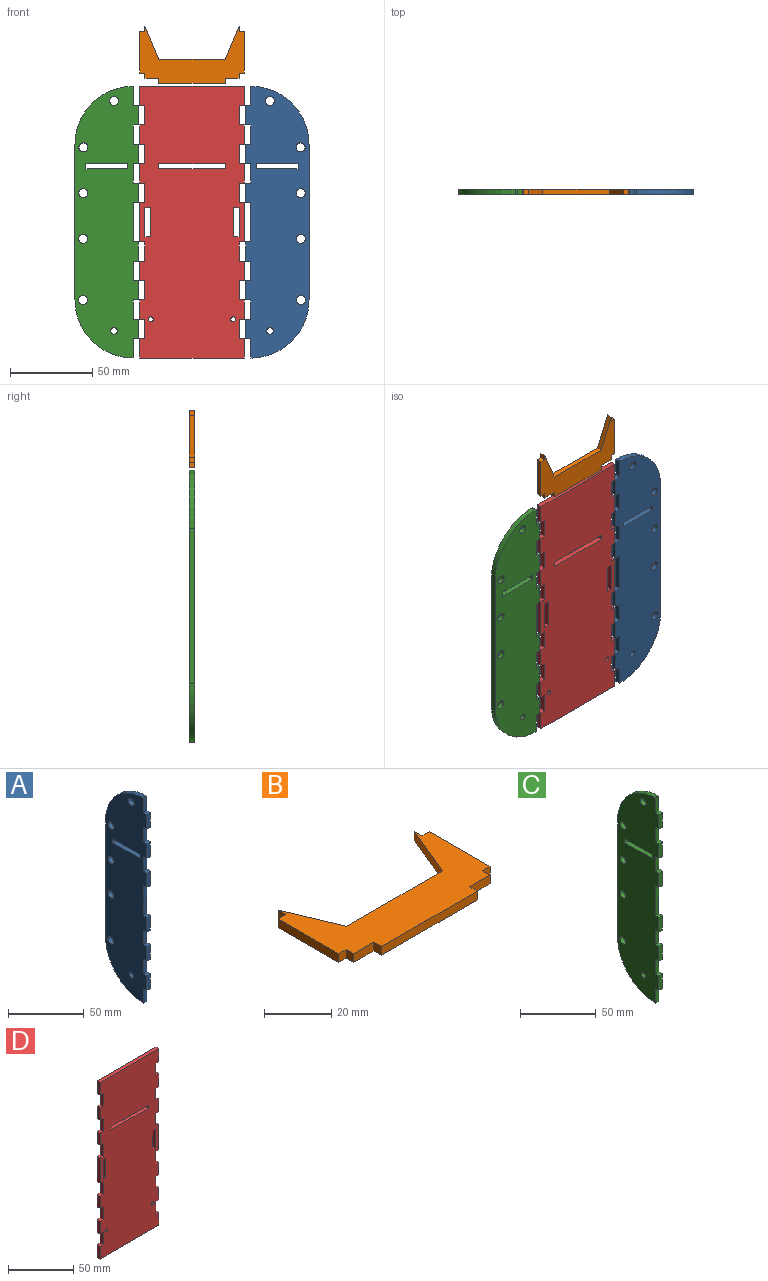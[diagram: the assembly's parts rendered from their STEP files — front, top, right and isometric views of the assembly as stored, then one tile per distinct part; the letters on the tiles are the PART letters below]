
ASSEMBLY  parts=4 mates=5
PART A: 42 faces, bbox 3.2x38.5x165.1 mm
  f0: plane 165.1x38.45mm, normal (1,0,0), area 5303.1mm2, adj f1,f2,f3,f4,f5,f6,f7,f8
  f1: plane 3.18x3.18mm, normal (0,0,1), area 10.1mm2, adj f0,f2,f28,f31
  f2: plane 11.76x3.18mm, normal (0,-1,0), area 37.3mm2, adj f0,f1,f3,f28
  f3: plane 3.18x3.18mm, normal (0,0,-1), area 10.1mm2, adj f0,f2,f4,f28
  f4: plane 11.76x3.18mm, normal (0,-1,0), area 37.3mm2, adj f0,f3,f5,f28
  f5: plane 3.18x3.18mm, normal (0,0,1), area 10.1mm2, adj f0,f4,f6,f28
  f6: plane 11.76x3.18mm, normal (0,-1,0), area 37.3mm2, adj f0,f5,f7,f28
  f7: plane 3.18x3.18mm, normal (0,0,-1), area 10.1mm2, adj f0,f6,f8,f28
  f8: plane 11.76x3.18mm, normal (0,-1,0), area 37.3mm2, adj f0,f7,f9,f28
  f9: plane 3.18x0.97mm, normal (0,0,-1), area 3.1mm2, adj f0,f8,f10,f28
  f10: cylinder r=35.28mm len=35.27mm, axis (-1,0,0), area 172.9mm2, adj f0,f9,f11,f28
  f11: plane 94.57x3.18mm, normal (0,1,0), area 300.3mm2, adj f0,f10,f12,f28
  f12: cylinder r=35.28mm len=35.27mm, axis (-1,0,0), area 172.9mm2, adj f0,f11,f13,f28
  f13: plane 3.18x0.97mm, normal (0,0,1), area 3.1mm2, adj f0,f12,f14,f28
  f14: plane 11.76x3.18mm, normal (0,-1,0), area 37.3mm2, adj f0,f13,f15,f28
  f15: plane 3.18x3.18mm, normal (0,0,1), area 10.1mm2, adj f0,f14,f16,f28
  f16: plane 11.76x3.18mm, normal (0,-1,0), area 37.3mm2, adj f0,f15,f17,f28
  f17: plane 3.18x3.18mm, normal (0,0,-1), area 10.1mm2, adj f0,f16,f18,f28
  f18: plane 11.76x3.18mm, normal (0,-1,0), area 37.3mm2, adj f0,f17,f19,f28
  f19: plane 3.18x3.18mm, normal (0,0,1), area 10.1mm2, adj f0,f18,f20,f28
  f20: plane 11.76x3.18mm, normal (0,-1,0), area 37.3mm2, adj f0,f19,f21,f28
  f21: plane 3.18x3.18mm, normal (0,0,-1), area 10.1mm2, adj f0,f20,f22,f28
  f22: plane 11.76x3.18mm, normal (0,-1,0), area 37.3mm2, adj f0,f21,f23,f28
  f23: plane 3.18x3.18mm, normal (0,0,1), area 10.1mm2, adj f0,f22,f24,f28
  f24: plane 11.76x3.18mm, normal (0,-1,0), area 37.3mm2, adj f0,f23,f25,f28
  f25: plane 3.18x3.18mm, normal (0,0,-1), area 10.1mm2, adj f0,f24,f26,f28
  f26: plane 24.04x3.18mm, normal (0,-1,0), area 76.3mm2, adj f0,f25,f27,f28
  f27: plane 3.18x3.18mm, normal (0,0,1), area 10.1mm2, adj f0,f26,f28,f30
  f28: plane 165.1x38.45mm, normal (-1,0,0), area 5303.1mm2, adj f1,f2,f3,f4,f5,f6,f7,f8
  f29: cylinder r=2.75mm len=5.5mm, axis (-1,0,0), area 54.9mm2, adj f0,f28
  f30: plane 11.76x3.18mm, normal (0,-1,0), area 37.3mm2, adj f0,f27,f28,f32
  f31: plane 11.76x3.18mm, normal (0,-1,0), area 37.3mm2, adj f0,f1,f28,f32
  f32: plane 3.18x3.18mm, normal (0,0,-1), area 10.1mm2, adj f0,f28,f30,f31
  f33: cylinder r=2.75mm len=5.5mm, axis (-1,0,0), area 54.9mm2, adj f0,f28
  f34: cylinder r=2mm len=4mm, axis (-1,0,0), area 39.9mm2, adj f0,f28
  f35: cylinder r=2.75mm len=5.5mm, axis (-1,0,0), area 54.9mm2, adj f0,f28
  f36: cylinder r=2.75mm len=5.5mm, axis (-1,0,0), area 54.9mm2, adj f0,f28
  f37: cylinder r=2.75mm len=5.5mm, axis (-1,0,0), area 54.9mm2, adj f0,f28
  f38: plane 25.4x3.18mm, normal (0,0,1), area 80.6mm2, adj f0,f28,f40,f41
  f39: plane 25.4x3.18mm, normal (0,0,-1), area 80.6mm2, adj f0,f28,f40,f41
  f40: plane 3.18x3.18mm, normal (0,1,0), area 10.1mm2, adj f0,f28,f38,f39
  f41: plane 3.18x3.18mm, normal (0,-1,0), area 10.1mm2, adj f0,f28,f38,f39
PART B: 20 faces, bbox 63.5x34.9x3.2 mm
  f0: plane 63.5x34.93mm, normal (0,0,-1), area 1117.7mm2, adj f2,f3,f4,f5,f6,f7,f8,f9
  f1: plane 63.5x34.93mm, normal (0,0,1), area 1117.7mm2, adj f2,f3,f4,f5,f6,f7,f8,f9
  f2: plane 20.25x8.47mm, normal (0.92,0.39,0), area 69.7mm2, adj f0,f1,f3,f18
  f3: plane 3.18x3.18mm, normal (-1,0,0), area 10.1mm2, adj f0,f1,f2,f4
  f4: plane 3.18x3.18mm, normal (0,1,0), area 10.1mm2, adj f0,f1,f3,f5
  f5: plane 25.4x3.18mm, normal (-1,0,0), area 80.6mm2, adj f0,f1,f4,f6
  f6: plane 3.18x3.18mm, normal (0,-1,0), area 10.1mm2, adj f0,f1,f5,f7
  f7: plane 3.18x3.18mm, normal (-1,0,0), area 10.1mm2, adj f0,f1,f6,f8
  f8: plane 8.47x3.18mm, normal (0,-1,0), area 26.9mm2, adj f0,f1,f7,f9
  f9: plane 3.18x3.18mm, normal (-1,0,0), area 10.1mm2, adj f0,f1,f8,f10
  f10: plane 40.22x3.18mm, normal (0,-1,0), area 127.7mm2, adj f0,f1,f9,f11
  f11: plane 3.18x3.18mm, normal (1,0,0), area 10.1mm2, adj f0,f1,f10,f12
  f12: plane 8.47x3.18mm, normal (0,-1,0), area 26.9mm2, adj f0,f1,f11,f13
  f13: plane 3.18x3.18mm, normal (1,0,0), area 10.1mm2, adj f0,f1,f12,f14
  f14: plane 3.18x3.18mm, normal (0,-1,0), area 10.1mm2, adj f0,f1,f13,f15
  f15: plane 25.4x3.18mm, normal (1,0,0), area 80.6mm2, adj f0,f1,f14,f16
  f16: plane 3.18x3.18mm, normal (0,1,0), area 10.1mm2, adj f0,f1,f15,f17
  f17: plane 3.18x3.18mm, normal (1,0,0), area 10.1mm2, adj f0,f1,f16,f19
  f18: plane 40.22x3.18mm, normal (0,1,0), area 127.7mm2, adj f0,f1,f2,f19
  f19: plane 20.25x8.47mm, normal (-0.92,0.39,0), area 69.7mm2, adj f0,f1,f17,f18
PART C: 42 faces, bbox 3.2x38.5x165.1 mm
  f0: plane 165.1x38.45mm, normal (-1,0,0), area 5303.1mm2, adj f1,f2,f3,f4,f5,f6,f7,f8
  f1: plane 3.18x3.18mm, normal (0,0,1), area 10.1mm2, adj f0,f2,f28,f31
  f2: plane 11.76x3.18mm, normal (0,-1,0), area 37.3mm2, adj f0,f1,f3,f28
  f3: plane 3.18x3.18mm, normal (0,0,-1), area 10.1mm2, adj f0,f2,f4,f28
  f4: plane 11.76x3.18mm, normal (0,-1,0), area 37.3mm2, adj f0,f3,f5,f28
  f5: plane 3.18x3.18mm, normal (0,0,1), area 10.1mm2, adj f0,f4,f6,f28
  f6: plane 11.76x3.18mm, normal (0,-1,0), area 37.3mm2, adj f0,f5,f7,f28
  f7: plane 3.18x3.18mm, normal (0,0,-1), area 10.1mm2, adj f0,f6,f8,f28
  f8: plane 11.76x3.18mm, normal (0,-1,0), area 37.3mm2, adj f0,f7,f9,f28
  f9: plane 3.18x0.97mm, normal (0,0,-1), area 3.1mm2, adj f0,f8,f10,f28
  f10: cylinder r=35.28mm len=35.27mm, axis (1,0,0), area 172.9mm2, adj f0,f9,f11,f28
  f11: plane 94.57x3.18mm, normal (0,1,0), area 300.3mm2, adj f0,f10,f12,f28
  f12: cylinder r=35.28mm len=35.27mm, axis (1,0,0), area 172.9mm2, adj f0,f11,f13,f28
  f13: plane 3.18x0.97mm, normal (0,0,1), area 3.1mm2, adj f0,f12,f14,f28
  f14: plane 11.76x3.18mm, normal (0,-1,0), area 37.3mm2, adj f0,f13,f15,f28
  f15: plane 3.18x3.18mm, normal (0,0,1), area 10.1mm2, adj f0,f14,f16,f28
  f16: plane 11.76x3.18mm, normal (0,-1,0), area 37.3mm2, adj f0,f15,f17,f28
  f17: plane 3.18x3.18mm, normal (0,0,-1), area 10.1mm2, adj f0,f16,f18,f28
  f18: plane 11.76x3.18mm, normal (0,-1,0), area 37.3mm2, adj f0,f17,f19,f28
  f19: plane 3.18x3.18mm, normal (0,0,1), area 10.1mm2, adj f0,f18,f20,f28
  f20: plane 11.76x3.18mm, normal (0,-1,0), area 37.3mm2, adj f0,f19,f21,f28
  f21: plane 3.18x3.18mm, normal (0,0,-1), area 10.1mm2, adj f0,f20,f22,f28
  f22: plane 11.76x3.18mm, normal (0,-1,0), area 37.3mm2, adj f0,f21,f23,f28
  f23: plane 3.18x3.18mm, normal (0,0,1), area 10.1mm2, adj f0,f22,f24,f28
  f24: plane 11.76x3.18mm, normal (0,-1,0), area 37.3mm2, adj f0,f23,f25,f28
  f25: plane 3.18x3.18mm, normal (0,0,-1), area 10.1mm2, adj f0,f24,f26,f28
  f26: plane 24.04x3.18mm, normal (0,-1,0), area 76.3mm2, adj f0,f25,f27,f28
  f27: plane 3.18x3.18mm, normal (0,0,1), area 10.1mm2, adj f0,f26,f28,f30
  f28: plane 165.1x38.45mm, normal (1,0,0), area 5303.1mm2, adj f1,f2,f3,f4,f5,f6,f7,f8
  f29: cylinder r=2.75mm len=5.5mm, axis (1,0,0), area 54.9mm2, adj f0,f28
  f30: plane 11.76x3.18mm, normal (0,-1,0), area 37.3mm2, adj f0,f27,f28,f32
  f31: plane 11.76x3.18mm, normal (0,-1,0), area 37.3mm2, adj f0,f1,f28,f32
  f32: plane 3.18x3.18mm, normal (0,0,-1), area 10.1mm2, adj f0,f28,f30,f31
  f33: cylinder r=2.75mm len=5.5mm, axis (1,0,0), area 54.9mm2, adj f0,f28
  f34: cylinder r=2mm len=4mm, axis (1,0,0), area 39.9mm2, adj f0,f28
  f35: cylinder r=2.75mm len=5.5mm, axis (1,0,0), area 54.9mm2, adj f0,f28
  f36: cylinder r=2.75mm len=5.5mm, axis (1,0,0), area 54.9mm2, adj f0,f28
  f37: cylinder r=2.75mm len=5.5mm, axis (1,0,0), area 54.9mm2, adj f0,f28
  f38: plane 25.4x3.18mm, normal (0,0,1), area 80.6mm2, adj f0,f28,f40,f41
  f39: plane 25.4x3.18mm, normal (0,0,-1), area 80.6mm2, adj f0,f28,f40,f41
  f40: plane 3.18x3.18mm, normal (0,-1,0), area 10.1mm2, adj f0,f28,f38,f39
  f41: plane 3.18x3.18mm, normal (0,1,0), area 10.1mm2, adj f0,f28,f38,f39
PART D: 68 faces, bbox 63.5x3.2x165.1 mm
  f0: plane 11.76x3.18mm, normal (1,0,0), area 37.3mm2, adj f1,f58,f62,f63
  f1: plane 63.5x3.18mm, normal (0,0,1), area 201.6mm2, adj f0,f2,f62,f63
  f2: plane 11.76x3.18mm, normal (-1,0,0), area 37.3mm2, adj f1,f3,f62,f63
  f3: plane 3.18x3.18mm, normal (0,0,-1), area 10.1mm2, adj f2,f4,f62,f63
  f4: plane 11.76x3.18mm, normal (-1,0,0), area 37.3mm2, adj f3,f5,f62,f63
  f5: plane 3.18x3.18mm, normal (0,0,1), area 10.1mm2, adj f4,f6,f62,f63
  f6: plane 11.76x3.18mm, normal (-1,0,0), area 37.3mm2, adj f5,f7,f62,f63
  f7: plane 3.18x3.18mm, normal (0,0,-1), area 10.1mm2, adj f6,f8,f62,f63
  f8: plane 11.76x3.18mm, normal (-1,0,0), area 37.3mm2, adj f7,f9,f62,f63
  f9: plane 3.18x3.18mm, normal (0,0,1), area 10.1mm2, adj f8,f10,f62,f63
  f10: plane 11.76x3.18mm, normal (-1,0,0), area 37.3mm2, adj f9,f11,f62,f63
  f11: plane 3.18x3.18mm, normal (0,0,-1), area 10.1mm2, adj f10,f12,f62,f63
  f12: plane 11.76x3.18mm, normal (-1,0,0), area 37.3mm2, adj f11,f13,f62,f63
  f13: plane 3.18x3.18mm, normal (0,0,1), area 10.1mm2, adj f12,f14,f62,f63
  f14: plane 24.04x3.18mm, normal (-1,0,0), area 76.3mm2, adj f13,f15,f62,f63
  f15: plane 3.18x3.18mm, normal (0,0,-1), area 10.1mm2, adj f14,f16,f62,f63
  f16: plane 11.76x3.18mm, normal (-1,0,0), area 37.3mm2, adj f15,f17,f62,f63
  f17: plane 3.18x3.18mm, normal (0,0,1), area 10.1mm2, adj f16,f18,f62,f63
  f18: plane 11.76x3.18mm, normal (-1,0,0), area 37.3mm2, adj f17,f19,f62,f63
  f19: plane 3.18x3.18mm, normal (0,0,-1), area 10.1mm2, adj f18,f20,f62,f63
  f20: plane 11.76x3.18mm, normal (-1,0,0), area 37.3mm2, adj f19,f21,f62,f63
  f21: plane 3.18x3.18mm, normal (0,0,1), area 10.1mm2, adj f20,f22,f62,f63
  f22: plane 11.76x3.18mm, normal (-1,0,0), area 37.3mm2, adj f21,f23,f62,f63
  f23: plane 3.18x3.18mm, normal (0,0,-1), area 10.1mm2, adj f22,f24,f62,f63
  f24: plane 11.76x3.18mm, normal (-1,0,0), area 37.3mm2, adj f23,f25,f62,f63
  f25: plane 3.18x3.18mm, normal (0,0,1), area 10.1mm2, adj f24,f26,f62,f63
  f26: plane 11.76x3.18mm, normal (-1,0,0), area 37.3mm2, adj f25,f27,f62,f63
  f27: plane 63.5x3.18mm, normal (0,0,-1), area 201.6mm2, adj f26,f28,f62,f63
  f28: plane 11.76x3.18mm, normal (1,0,0), area 37.3mm2, adj f27,f29,f62,f63
  f29: plane 3.18x3.18mm, normal (0,0,1), area 10.1mm2, adj f28,f30,f62,f63
  f30: plane 11.76x3.18mm, normal (1,0,0), area 37.3mm2, adj f29,f31,f62,f63
  f31: plane 3.18x3.18mm, normal (0,0,-1), area 10.1mm2, adj f30,f32,f62,f63
  f32: plane 11.76x3.18mm, normal (1,0,0), area 37.3mm2, adj f31,f33,f62,f63
  f33: plane 3.18x3.18mm, normal (0,0,1), area 10.1mm2, adj f32,f34,f62,f63
  f34: plane 11.76x3.18mm, normal (1,0,0), area 37.3mm2, adj f33,f35,f62,f63
  f35: plane 3.18x3.18mm, normal (0,0,-1), area 10.1mm2, adj f34,f36,f62,f63
  f36: plane 11.76x3.18mm, normal (1,0,0), area 37.3mm2, adj f35,f37,f62,f63
  f37: plane 3.18x3.18mm, normal (0,0,1), area 10.1mm2, adj f36,f38,f62,f63
  f38: plane 11.76x3.18mm, normal (1,0,0), area 37.3mm2, adj f37,f39,f62,f63
  f39: plane 3.18x3.18mm, normal (0,0,-1), area 10.1mm2, adj f38,f40,f62,f63
  f40: plane 24.04x3.18mm, normal (1,0,0), area 76.3mm2, adj f39,f41,f62,f63
  f41: plane 3.18x3.18mm, normal (0,0,1), area 10.1mm2, adj f40,f42,f62,f63
  f42: plane 11.76x3.18mm, normal (1,0,0), area 37.3mm2, adj f41,f43,f62,f63
  f43: plane 3.18x3.18mm, normal (0,0,-1), area 10.1mm2, adj f42,f44,f62,f63
  f44: plane 11.76x3.18mm, normal (1,0,0), area 37.3mm2, adj f43,f45,f62,f63
  f45: plane 3.18x3.18mm, normal (0,0,1), area 10.1mm2, adj f44,f46,f62,f63
  f46: plane 11.76x3.18mm, normal (1,0,0), area 37.3mm2, adj f45,f47,f62,f63
  f47: plane 3.18x3.18mm, normal (0,0,-1), area 10.1mm2, adj f46,f48,f62,f63
  f48: plane 11.76x3.18mm, normal (1,0,0), area 37.3mm2, adj f47,f49,f62,f63
  f49: plane 3.18x3.18mm, normal (0,0,1), area 10.1mm2, adj f48,f50,f62,f63
  f50: plane 11.76x3.18mm, normal (1,0,0), area 37.3mm2, adj f49,f58,f62,f63
  f51: plane 3.18x3.18mm, normal (0,0,-1), area 10.1mm2, adj f52,f59,f62,f63
  f52: plane 17.69x3.18mm, normal (-1,0,0), area 56.2mm2, adj f51,f53,f62,f63
  f53: plane 3.18x3.18mm, normal (0,0,1), area 10.1mm2, adj f52,f59,f62,f63
  f54: plane 17.69x3.18mm, normal (1,0,0), area 56.2mm2, adj f55,f60,f62,f63
  f55: plane 3.18x3.18mm, normal (0,0,-1), area 10.1mm2, adj f54,f56,f62,f63
  f56: plane 17.69x3.18mm, normal (-1,0,0), area 56.2mm2, adj f55,f60,f62,f63
  f57: cylinder r=1.5mm len=3.18mm, axis (0,1,0), area 29.9mm2, adj f62,f63
  f58: plane 3.18x3.18mm, normal (0,0,-1), area 10.1mm2, adj f0,f50,f62,f63
  f59: plane 17.69x3.18mm, normal (1,0,0), area 56.2mm2, adj f51,f53,f62,f63
  f60: plane 3.18x3.18mm, normal (0,0,1), area 10.1mm2, adj f54,f56,f62,f63
  f61: cylinder r=1.5mm len=3.18mm, axis (0,1,0), area 29.9mm2, adj f62,f63
  f62: plane 165.1x63.5mm, normal (0,-1,0), area 9781.8mm2, adj f0,f1,f2,f3,f4,f5,f6,f7
  f63: plane 165.1x63.5mm, normal (0,1,0), area 9781.8mm2, adj f0,f1,f2,f3,f4,f5,f6,f7
  f64: plane 40.22x3.18mm, normal (0,0,1), area 127.7mm2, adj f62,f63,f66,f67
  f65: plane 40.22x3.18mm, normal (0,0,-1), area 127.7mm2, adj f62,f63,f66,f67
  f66: plane 3.18x3.18mm, normal (1,0,0), area 10.1mm2, adj f62,f63,f64,f65
  f67: plane 3.18x3.18mm, normal (-1,0,0), area 10.1mm2, adj f62,f63,f64,f65
PLACE A rot(axis=(0,0,-1),90deg) t=(-9.63,34.16,-13.67)mm
PLACE B rot(axis=(1,0,0),90deg) t=(-45.47,96.98,132.82)mm
PLACE C rot(axis=(0,0,1),90deg) t=(-81.31,34.16,-13.67)mm
PLACE D t=(-45.47,5.58,-13.67)mm fixed
MATE planar B.f15 <-> D.f0  axis (1,0,0) through (-13.72,4,148.7)mm
MATE planar D.f62 <-> C.f0  axis (0,-1,0) through (-16.9,2.41,104.41)mm
MATE planar D.f62 <-> B.f1  axis (0,-1,0) through (-45.47,2.41,45.02)mm
MATE planar D.f62 <-> A.f0  axis (0,-1,0) through (-45.47,2.41,45.02)mm
MATE parallel D.f40 <-> A.f16  axis (1,0,0) through (-13.72,4,45.37)mm
